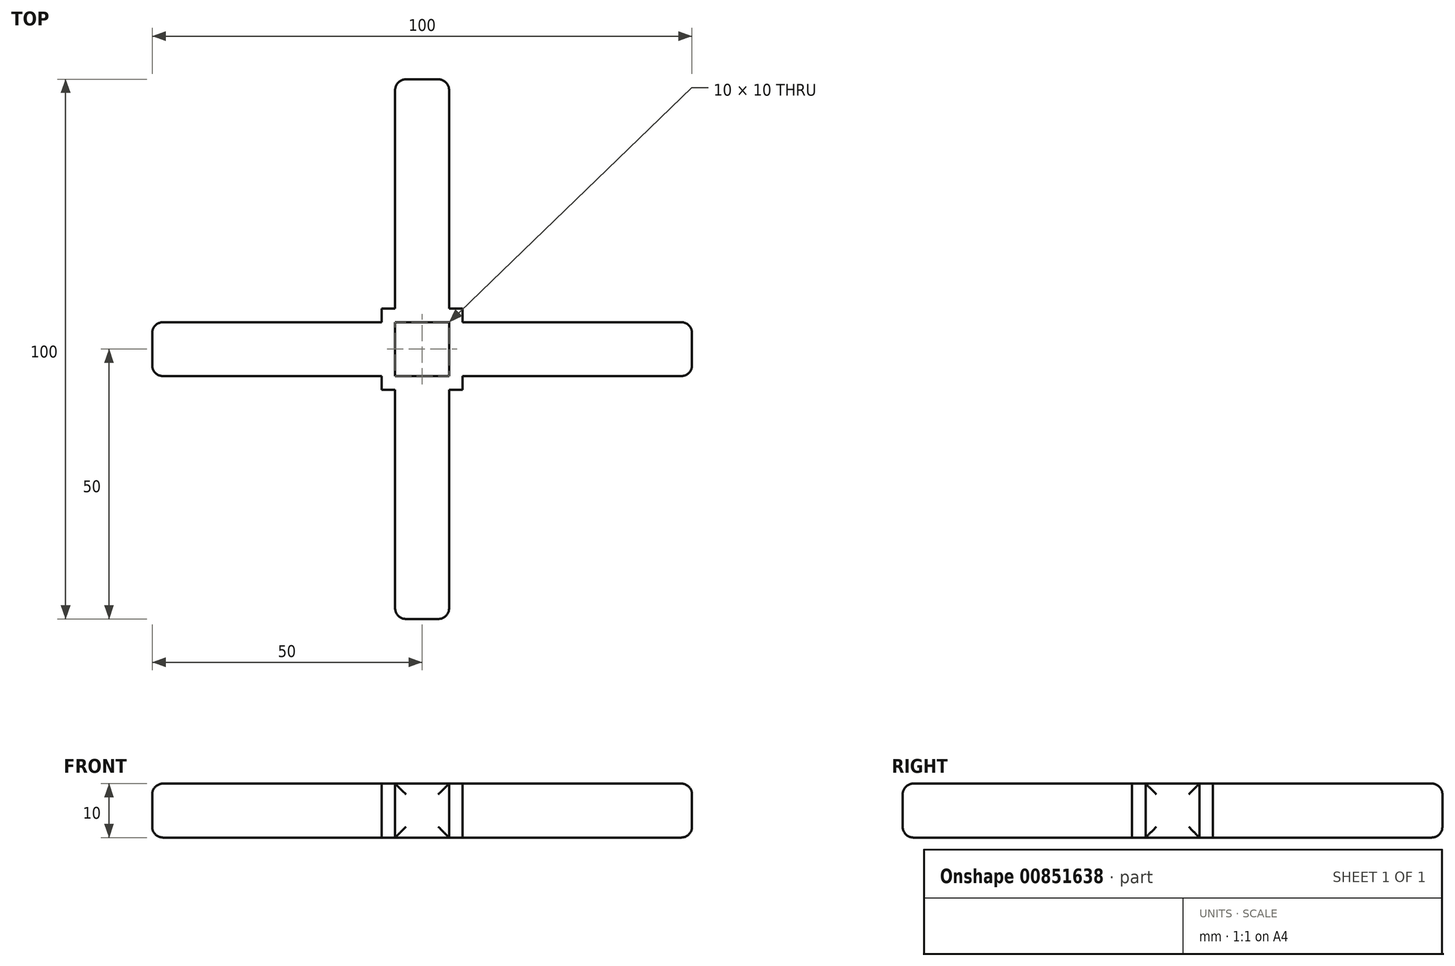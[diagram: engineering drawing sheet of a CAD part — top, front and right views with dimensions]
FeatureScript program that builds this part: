
annotation { "Feature Type Name" : "Feature", "Feature Type Description" : "" }
export const myFeature = defineFeature(function(context is Context, id is Id, definition is map)
    precondition{}
    {
        {
            assignVariable(context, id + "F0", {"name" : "width", "anyValue" : 10 * mm});
        }
        {
            var Q0;
            Q0=qCreatedBy(makeId("Top.planeOp"),FACE);
            var sketch = newSketch(context, id + "F1", { "sketchPlane" : qUnion([Q0])});
            skLineSegment(sketch, "E0.bottom", {"start": v(50, 5) * mm, "end": v(-50, 5) * mm});
            skLineSegment(sketch, "E0.top", {"start": v(50, -5) * mm, "end": v(-50, -5) * mm});
            skLineSegment(sketch, "E0.left", {"start": v(50, 5) * mm, "end": v(50, -5) * mm});
            skLineSegment(sketch, "E0.right", {"start": v(-50, 5) * mm, "end": v(-50, -5) * mm});
            skPoint(sketch, "E0.middle", {"position": v(0, 0) * mm});
            skSolve(sketch);
        }
        {
            var Q0;
            Q0 = qSketchRegion(id + "F1", true);
            extrude(context, id + "F2", {"entities" : qUnion([Q0]), "depth" : getVariable(context, 'width'), "offsetDistance" : 25.4 * mm});
        }
        {
            var Q0;
            Q0=makeQuery(id+"F2.opExtrude","SWEPT_FACE",FACE,{"disambiguationData":[OSD([sQuery(id+"F1.wireOp",EDGE,"E0.left")])]});
            var Q1;
            Q1=makeQuery(id+"F2.opExtrude","SWEPT_FACE",FACE,{"disambiguationData":[OSD([sQuery(id+"F1.wireOp",EDGE,"E0.right")])]});
            fillet(context, id + "F3", {"entities" : qUnion([Q0, Q1]), "radius" : 2 * mm, "tangentPropagation" : true, "allowEdgeOverflow" : false});
        }
        {
            var Q0;
            Q0=qCreatedBy(makeId("Front.planeOp"),FACE);
            var sketch = newSketch(context, id + "F4", { "sketchPlane" : qUnion([Q0])});
            skLineSegment(sketch, "E1", {"start": v(0, 0) * mm, "end": v(0, 35.9) * mm, "construction": true});
            skSolve(sketch);
        }
        {
            var Q0;
            Q0=makeQuery(id+"F2.opExtrude","SWEPT_BODY",BODY,{"disambiguationData":[OSD([sQuery(id+"F1.wireOp",EDGE,"E0.bottom"),sQuery(id+"F1.wireOp",EDGE,"E0.top"),sQuery(id+"F1.wireOp",EDGE,"E0.left"),sQuery(id+"F1.wireOp",EDGE,"E0.right")])]});
            var Q1;
            Q1=sQuery(id+"F4.wireOp",EDGE,"E1");
            circularPattern(context, id + "F5", {"operationType" : NewBodyOperationType.ADD, "entities" : qUnion([Q0]), "axis" : qUnion([Q1]), "angle" : 360 * degree, "instanceCount" : 4, "equalSpace" : true});
        }
        {
            var Q0;
            Q0=qCreatedBy(makeId("Top.planeOp"),FACE);
            var sketch = newSketch(context, id + "F6", { "sketchPlane" : qUnion([Q0])});
            skLineSegment(sketch, "E2.bottom", {"start": v(7.5, 7.5) * mm, "end": v(-7.5, 7.5) * mm});
            skLineSegment(sketch, "E2.top", {"start": v(7.5, -7.5) * mm, "end": v(-7.5, -7.5) * mm});
            skLineSegment(sketch, "E2.left", {"start": v(7.5, 7.5) * mm, "end": v(7.5, -7.5) * mm});
            skLineSegment(sketch, "E2.right", {"start": v(-7.5, 7.5) * mm, "end": v(-7.5, -7.5) * mm});
            skPoint(sketch, "E2.middle", {"position": v(0, 0) * mm});
            skLineSegment(sketch, "E3.bottom", {"start": v(5, 5) * mm, "end": v(-5, 5) * mm});
            skLineSegment(sketch, "E3.top", {"start": v(5, -5) * mm, "end": v(-5, -5) * mm});
            skLineSegment(sketch, "E3.left", {"start": v(5, 5) * mm, "end": v(5, -5) * mm});
            skLineSegment(sketch, "E3.right", {"start": v(-5, 5) * mm, "end": v(-5, -5) * mm});
            skSolve(sketch);
        }
        {
            var Q0;
            Q0=makeQuery(id+"F6.imprint","IMPRINT",FACE,{"disambiguationData":[TD([[makeQuery(id+"F6.imprint","IMPRINT",EDGE,{"derivedFrom":sQuery(id+"F6.wireOp",EDGE,"E2.bottom")}),1.0]])]});
            extrude(context, id + "F7", {"entities" : qUnion([Q0]), "operationType" : NewBodyOperationType.ADD, "depth" : getVariable(context, 'width'), "offsetDistance" : 25.4 * mm});
        }
        {
            var Q0;
            Q0=makeQuery(id+"F6.imprint","IMPRINT",FACE,{"disambiguationData":[TD([[makeQuery(id+"F6.imprint","IMPRINT",EDGE,{"derivedFrom":sQuery(id+"F6.wireOp",EDGE,"E3.bottom")}),1.0]])]});
            extrude(context, id + "F8", {"entities" : qUnion([Q0]), "operationType" : NewBodyOperationType.REMOVE, "depth" : 25.4 * mm, "offsetDistance" : 25.4 * mm});
        }
    });
